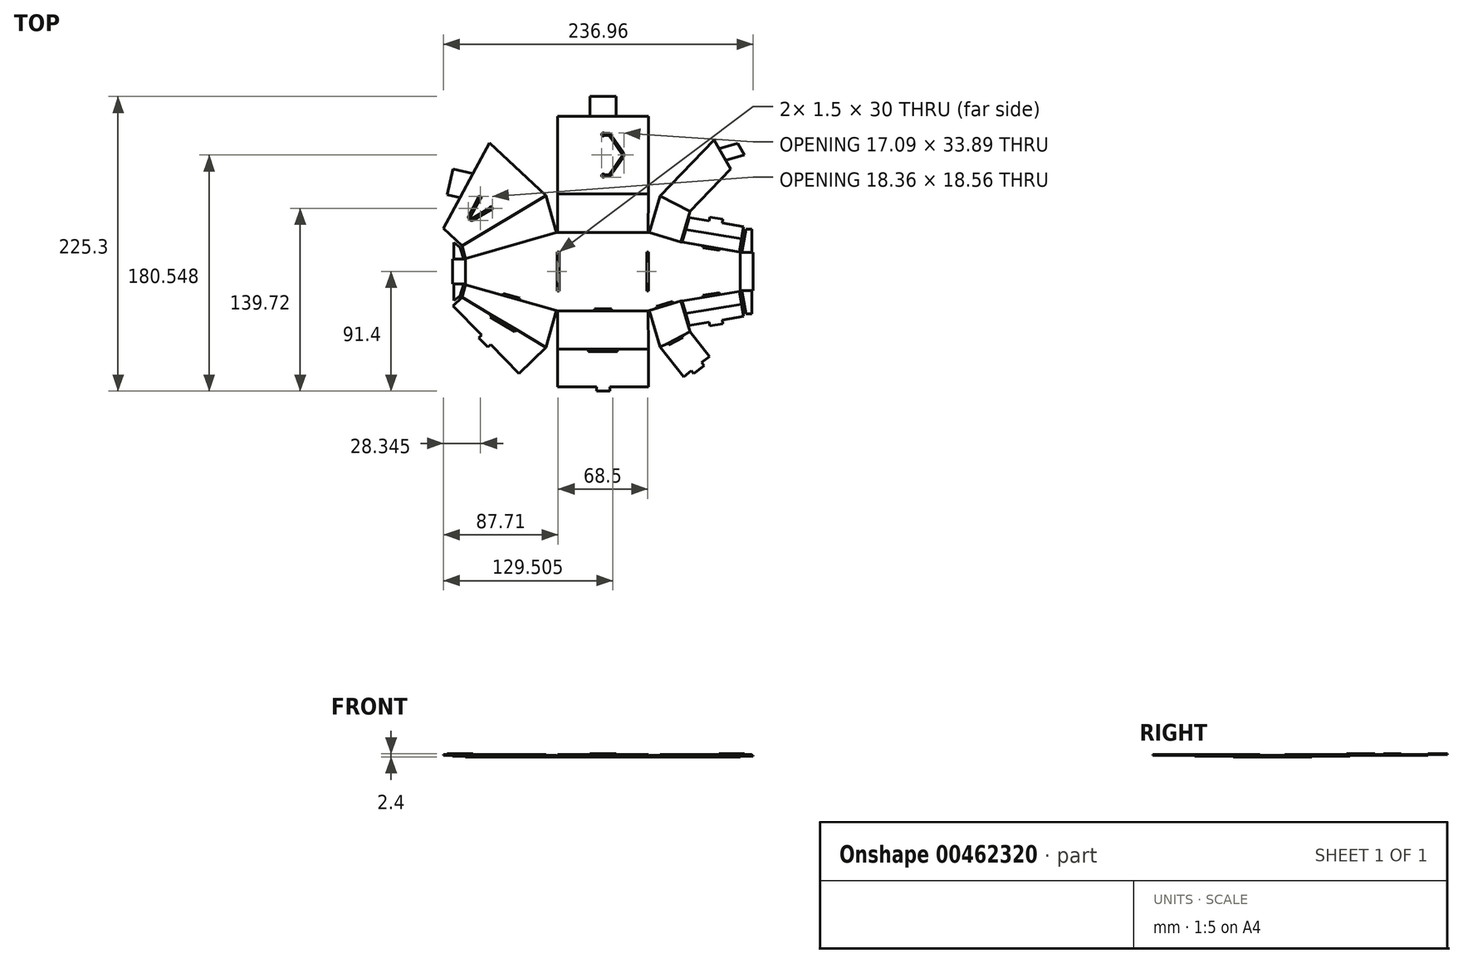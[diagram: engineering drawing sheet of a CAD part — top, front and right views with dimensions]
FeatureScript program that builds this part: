
annotation { "Feature Type Name" : "Feature", "Feature Type Description" : "" }
export const myFeature = defineFeature(function(context is Context, id is Id, definition is map)
    precondition{}
    {
        {
            var Q0;
            Q0=qCreatedBy(makeId("Top.planeOp"),FACE);
            var sketch = newSketch(context, id + "F0", { "sketchPlane" : qUnion([Q0])});
            skLineSegment(sketch, "E0.bottom", {"start": v(-35, 30) * mm, "end": v(35, 30) * mm});
            skLineSegment(sketch, "E0.top", {"start": v(-35, -30) * mm, "end": v(35, -30) * mm});
            skPoint(sketch, "E0.middle", {"position": v(0, 0) * mm});
            skLineSegment(sketch, "E1", {"start": v(-105, 0) * mm, "end": v(-105, 10) * mm});
            skLineSegment(sketch, "E2", {"start": v(-105, 10) * mm, "end": v(-35, 30) * mm});
            skLineSegment(sketch, "E3", {"start": v(-105, 0) * mm, "end": v(-105, -10) * mm});
            skLineSegment(sketch, "E4", {"start": v(-105, -10) * mm, "end": v(-35, -30) * mm});
            skLineSegment(sketch, "E5", {"start": v(60, -22.5) * mm, "end": v(35, -30) * mm});
            skLineSegment(sketch, "E6", {"start": v(60, 22.5) * mm, "end": v(35, 30) * mm});
            skLineSegment(sketch, "E7", {"start": v(105, 0) * mm, "end": v(105, 15) * mm});
            skLineSegment(sketch, "E8", {"start": v(105, 15) * mm, "end": v(60, 22.5) * mm});
            skLineSegment(sketch, "E9", {"start": v(105, 0) * mm, "end": v(105, -15) * mm});
            skLineSegment(sketch, "E10", {"start": v(105, -15) * mm, "end": v(60, -22.5) * mm});
            skSolve(sketch);
        }
        {
            var Q0;
            Q0 = qSketchRegion(id + "F0", true);
            extrude(context, id + "F1", {"entities" : qUnion([Q0]), "oppositeDirection" : true, "depth" : .6 * mm});
        }
        {
            var Q0;
            Q0=makeQuery(id+"F1.opExtrude","CAP_FACE",FACE,{"disambiguationData":[OSD([sQuery(id+"F0.wireOp",EDGE,"E0.bottom"),sQuery(id+"F0.wireOp",EDGE,"E0.top"),sQuery(id+"F0.wireOp",EDGE,"E1"),sQuery(id+"F0.wireOp",EDGE,"E2"),sQuery(id+"F0.wireOp",EDGE,"E3"),sQuery(id+"F0.wireOp",EDGE,"E4"),sQuery(id+"F0.wireOp",EDGE,"E5"),sQuery(id+"F0.wireOp",EDGE,"E6"),sQuery(id+"F0.wireOp",EDGE,"E7"),sQuery(id+"F0.wireOp",EDGE,"E8"),sQuery(id+"F0.wireOp",EDGE,"E9"),sQuery(id+"F0.wireOp",EDGE,"E10")])],"isStart":true});
            var sketch = newSketch(context, id + "F2", { "sketchPlane" : qUnion([Q0])});
            skLineSegment(sketch, "E11.0", {"start": v(-105, -10) * mm, "end": v(-35.48, -29.86) * mm});
            skPoint(sketch, "E12.orphan", {"position": v(-35, -30) * mm});
            skLineSegment(sketch, "E13", {"start": v(-35.48, -29.86) * mm, "end": v(-43.52, -58) * mm});
            skLineSegment(sketch, "E14", {"start": v(-105, -10) * mm, "end": v(-107.75, -19.62) * mm});
            skLineSegment(sketch, "E15", {"start": v(-107.75, -19.62) * mm, "end": v(-43.52, -58) * mm});
            skPoint(sketch, "E16.0", {"position": v(-105, 0) * mm});
            skLineSegment(sketch, "E17.MirrorCS", {"start": v(-105, 10) * mm, "end": v(-35.48, 29.86) * mm});
            skLineSegment(sketch, "E18.MirrorCS", {"start": v(-35.48, 29.86) * mm, "end": v(-43.52, 58) * mm});
            skLineSegment(sketch, "E19.MirrorCS", {"start": v(-107.75, 19.62) * mm, "end": v(-43.52, 58) * mm});
            skLineSegment(sketch, "E20.MirrorCS", {"start": v(-105, 10) * mm, "end": v(-107.75, 19.62) * mm});
            skSolve(sketch);
        }
        {
            var Q0;
            Q0 = qSketchRegion(id + "F2", true);
            extrude(context, id + "F3", {"entities" : qUnion([Q0]), "depth" : .6 * mm});
        }
        {
            var Q0;
            Q0=makeQuery(id+"F1.opExtrude","CAP_FACE",FACE,{"disambiguationData":[OSD([sQuery(id+"F0.wireOp",EDGE,"E0.bottom"),sQuery(id+"F0.wireOp",EDGE,"E0.top"),sQuery(id+"F0.wireOp",EDGE,"E1"),sQuery(id+"F0.wireOp",EDGE,"E2"),sQuery(id+"F0.wireOp",EDGE,"E3"),sQuery(id+"F0.wireOp",EDGE,"E4"),sQuery(id+"F0.wireOp",EDGE,"E5"),sQuery(id+"F0.wireOp",EDGE,"E6"),sQuery(id+"F0.wireOp",EDGE,"E7"),sQuery(id+"F0.wireOp",EDGE,"E8"),sQuery(id+"F0.wireOp",EDGE,"E9"),sQuery(id+"F0.wireOp",EDGE,"E10")])],"isStart":true});
            var sketch = newSketch(context, id + "F4", { "sketchPlane" : qUnion([Q0])});
            skLineSegment(sketch, "E21", {"start": v(34.5, 30) * mm, "end": v(35, 59.4) * mm});
            skLineSegment(sketch, "E22", {"start": v(-34.5, 30) * mm, "end": v(-34.5, 59.4) * mm});
            skLineSegment(sketch, "E23", {"start": v(-34.5, 59.4) * mm, "end": v(35, 59.4) * mm});
            skLineSegment(sketch, "E24", {"start": v(-34.5, 30) * mm, "end": v(34.5, 30) * mm});
            skLineSegment(sketch, "E25.MirrorCS", {"start": v(-34.5, -30) * mm, "end": v(34.5, -30) * mm});
            skLineSegment(sketch, "E26.MirrorCS", {"start": v(-34.5, -30) * mm, "end": v(-34.5, -59.4) * mm});
            skLineSegment(sketch, "E27.MirrorCS", {"start": v(-34.5, -59.4) * mm, "end": v(35, -59.4) * mm});
            skLineSegment(sketch, "E28.MirrorCS", {"start": v(34.5, -30) * mm, "end": v(35, -59.4) * mm});
            skSolve(sketch);
        }
        {
            var Q0;
            Q0 = qSketchRegion(id + "F4", true);
            extrude(context, id + "F5", {"entities" : qUnion([Q0]), "depth" : .6 * mm});
        }
        {
            var Q0;
            Q0=makeQuery(id+"F1.opExtrude","CAP_FACE",FACE,{"disambiguationData":[OSD([sQuery(id+"F0.wireOp",EDGE,"E0.bottom"),sQuery(id+"F0.wireOp",EDGE,"E0.top"),sQuery(id+"F0.wireOp",EDGE,"E1"),sQuery(id+"F0.wireOp",EDGE,"E2"),sQuery(id+"F0.wireOp",EDGE,"E3"),sQuery(id+"F0.wireOp",EDGE,"E4"),sQuery(id+"F0.wireOp",EDGE,"E5"),sQuery(id+"F0.wireOp",EDGE,"E6"),sQuery(id+"F0.wireOp",EDGE,"E7"),sQuery(id+"F0.wireOp",EDGE,"E8"),sQuery(id+"F0.wireOp",EDGE,"E9"),sQuery(id+"F0.wireOp",EDGE,"E10")])],"isStart":true});
            var sketch = newSketch(context, id + "F6", { "sketchPlane" : qUnion([Q0])});
            skLineSegment(sketch, "E29", {"start": v(59.52, -22.64) * mm, "end": v(66.56, -46.11) * mm});
            skLineSegment(sketch, "E30", {"start": v(35.48, -29.86) * mm, "end": v(43.9, -57.92) * mm});
            skPoint(sketch, "E31.orphan", {"position": v(60, -22.5) * mm});
            skLineSegment(sketch, "E32", {"start": v(35.48, -29.86) * mm, "end": v(59.52, -22.64) * mm});
            skLineSegment(sketch, "E33", {"start": v(66.56, -46.11) * mm, "end": v(43.9, -57.92) * mm});
            skPoint(sketch, "E34.endSnap0", {"position": v(105, 0) * mm});
            skLineSegment(sketch, "E35.MirrorCS", {"start": v(59.52, 22.64) * mm, "end": v(66.56, 46.11) * mm});
            skPoint(sketch, "E36.MirrorP", {"position": v(60, 22.5) * mm});
            skLineSegment(sketch, "E37.MirrorCS", {"start": v(35.48, 29.86) * mm, "end": v(59.52, 22.64) * mm});
            skLineSegment(sketch, "E38.MirrorCS", {"start": v(66.56, 46.11) * mm, "end": v(43.9, 57.92) * mm});
            skLineSegment(sketch, "E39.MirrorCS", {"start": v(35.48, 29.86) * mm, "end": v(43.9, 57.92) * mm});
            skSolve(sketch);
        }
        {
            var Q0;
            Q0 = qSketchRegion(id + "F6", true);
            extrude(context, id + "F7", {"entities" : qUnion([Q0]), "depth" : .6 * mm});
        }
        {
            var Q0;
            Q0=makeQuery(id+"F1.opExtrude","CAP_FACE",FACE,{"disambiguationData":[OSD([sQuery(id+"F0.wireOp",EDGE,"E0.bottom"),sQuery(id+"F0.wireOp",EDGE,"E0.top"),sQuery(id+"F0.wireOp",EDGE,"E1"),sQuery(id+"F0.wireOp",EDGE,"E2"),sQuery(id+"F0.wireOp",EDGE,"E3"),sQuery(id+"F0.wireOp",EDGE,"E4"),sQuery(id+"F0.wireOp",EDGE,"E5"),sQuery(id+"F0.wireOp",EDGE,"E6"),sQuery(id+"F0.wireOp",EDGE,"E7"),sQuery(id+"F0.wireOp",EDGE,"E8"),sQuery(id+"F0.wireOp",EDGE,"E9"),sQuery(id+"F0.wireOp",EDGE,"E10")])],"isStart":true});
            var sketch = newSketch(context, id + "F8", { "sketchPlane" : qUnion([Q0])});
            skLineSegment(sketch, "E40", {"start": v(104.5, -15.08) * mm, "end": v(106.15, -24.95) * mm});
            skLineSegment(sketch, "E41", {"start": v(106.15, -24.95) * mm, "end": v(63.39, -32.07) * mm});
            skLineSegment(sketch, "E42", {"start": v(60.5, -22.42) * mm, "end": v(63.39, -32.07) * mm});
            skLineSegment(sketch, "E43", {"start": v(60.5, -22.42) * mm, "end": v(104.5, -15.08) * mm});
            skLineSegment(sketch, "E44.MirrorCS", {"start": v(104.5, 15.08) * mm, "end": v(106.15, 24.95) * mm});
            skLineSegment(sketch, "E45.MirrorCS", {"start": v(106.15, 24.95) * mm, "end": v(63.39, 32.07) * mm});
            skLineSegment(sketch, "E46.MirrorCS", {"start": v(60.5, 22.42) * mm, "end": v(63.39, 32.07) * mm});
            skLineSegment(sketch, "E47.MirrorCS", {"start": v(60.5, 22.42) * mm, "end": v(104.5, 15.08) * mm});
            skSolve(sketch);
        }
        {
            var Q0;
            Q0 = qSketchRegion(id + "F8", true);
            extrude(context, id + "F9", {"entities" : qUnion([Q0]), "depth" : .6 * mm});
        }
        {
            var Q0;
            Q0=makeQuery(id+"F1.opExtrude","CAP_FACE",FACE,{"disambiguationData":[OSD([sQuery(id+"F0.wireOp",EDGE,"E0.bottom"),sQuery(id+"F0.wireOp",EDGE,"E0.top"),sQuery(id+"F0.wireOp",EDGE,"E1"),sQuery(id+"F0.wireOp",EDGE,"E2"),sQuery(id+"F0.wireOp",EDGE,"E3"),sQuery(id+"F0.wireOp",EDGE,"E4"),sQuery(id+"F0.wireOp",EDGE,"E5"),sQuery(id+"F0.wireOp",EDGE,"E6"),sQuery(id+"F0.wireOp",EDGE,"E7"),sQuery(id+"F0.wireOp",EDGE,"E8"),sQuery(id+"F0.wireOp",EDGE,"E9"),sQuery(id+"F0.wireOp",EDGE,"E10")])],"isStart":true});
            var sketch = newSketch(context, id + "F10", { "sketchPlane" : qUnion([Q0])});
            skLineSegment(sketch, "E48", {"start": v(-105, -9.5) * mm, "end": v(-115, -9.5) * mm});
            skLineSegment(sketch, "E49", {"start": v(-105, 9.5) * mm, "end": v(-115, 9.5) * mm});
            skLineSegment(sketch, "E50", {"start": v(-115, 9.5) * mm, "end": v(-115, -9.5) * mm});
            skLineSegment(sketch, "E51", {"start": v(-105, 9.5) * mm, "end": v(-105, -9.5) * mm});
            skSolve(sketch);
        }
        {
            var Q0;
            Q0 = qSketchRegion(id + "F10", true);
            extrude(context, id + "F11", {"entities" : qUnion([Q0]), "depth" : .6 * mm});
        }
        {
            var Q0;
            Q0=makeQuery(id+"F1.opExtrude","CAP_FACE",FACE,{"disambiguationData":[OSD([sQuery(id+"F0.wireOp",EDGE,"E0.bottom"),sQuery(id+"F0.wireOp",EDGE,"E0.top"),sQuery(id+"F0.wireOp",EDGE,"E1"),sQuery(id+"F0.wireOp",EDGE,"E2"),sQuery(id+"F0.wireOp",EDGE,"E3"),sQuery(id+"F0.wireOp",EDGE,"E4"),sQuery(id+"F0.wireOp",EDGE,"E5"),sQuery(id+"F0.wireOp",EDGE,"E6"),sQuery(id+"F0.wireOp",EDGE,"E7"),sQuery(id+"F0.wireOp",EDGE,"E8"),sQuery(id+"F0.wireOp",EDGE,"E9"),sQuery(id+"F0.wireOp",EDGE,"E10")])],"isStart":true});
            var sketch = newSketch(context, id + "F12", { "sketchPlane" : qUnion([Q0])});
            skLineSegment(sketch, "E52.0", {"start": v(105, 14.5) * mm, "end": v(105, -14.5) * mm});
            skLineSegment(sketch, "E53", {"start": v(105, 14.5) * mm, "end": v(115, 14.5) * mm});
            skLineSegment(sketch, "E54", {"start": v(115, 14.5) * mm, "end": v(115, -14.5) * mm});
            skLineSegment(sketch, "E55", {"start": v(115, -14.5) * mm, "end": v(105, -14.5) * mm});
            skPoint(sketch, "E56.orphan", {"position": v(105, -15) * mm});
            skPoint(sketch, "E57.orphan", {"position": v(105, 15) * mm});
            skSolve(sketch);
        }
        {
            var Q0;
            Q0 = qSketchRegion(id + "F12", true);
            extrude(context, id + "F13", {"entities" : qUnion([Q0]), "depth" : .6 * mm});
        }
        {
            var Q0;
            Q0=makeQuery(id+"F9.opExtrude","CAP_FACE",FACE,{"disambiguationData":[OSD([sQuery(id+"F8.wireOp",EDGE,"E44.MirrorCS"),sQuery(id+"F8.wireOp",EDGE,"E45.MirrorCS"),sQuery(id+"F8.wireOp",EDGE,"E46.MirrorCS"),sQuery(id+"F8.wireOp",EDGE,"E47.MirrorCS")])],"isStart":false});
            var sketch = newSketch(context, id + "F14", { "sketchPlane" : qUnion([Q0])});
            skLineSegment(sketch, "E58.0", {"start": v(106.15, 24.95) * mm, "end": v(63.39, 32.07) * mm});
            skLineSegment(sketch, "E59", {"start": v(91.26, 37.06) * mm, "end": v(107.71, 34.32) * mm});
            skLineSegment(sketch, "E60", {"start": v(63.39, 32.07) * mm, "end": v(66.14, 41.25) * mm});
            skLineSegment(sketch, "E61", {"start": v(81.4, 38.7) * mm, "end": v(66.14, 41.25) * mm});
            skLineSegment(sketch, "E62", {"start": v(106.15, 24.95) * mm, "end": v(107.71, 34.32) * mm});
            skPoint(sketch, "E63.orphan", {"position": v(121.18, 32.07) * mm});
            skLineSegment(sketch, "E64.0", {"start": v(86.83, 40.84) * mm, "end": v(91.76, 40.02) * mm});
            skLineSegment(sketch, "E65.0", {"start": v(86.83, 40.84) * mm, "end": v(81.9, 41.66) * mm});
            skLineSegment(sketch, "E66.0", {"start": v(91.26, 37.06) * mm, "end": v(91.76, 40.02) * mm});
            skLineSegment(sketch, "E67.0", {"start": v(81.4, 38.7) * mm, "end": v(81.9, 41.66) * mm});
            skPoint(sketch, "E68.start.orphan", {"position": v(84.77, 28.5) * mm});
            skLineSegment(sketch, "E69.MirrorCS", {"start": v(91.26, -37.06) * mm, "end": v(91.76, -40.02) * mm});
            skLineSegment(sketch, "E70.MirrorCS", {"start": v(81.4, -38.7) * mm, "end": v(81.9, -41.66) * mm});
            skLineSegment(sketch, "E71.MirrorCS", {"start": v(106.15, -24.95) * mm, "end": v(107.71, -34.32) * mm});
            skLineSegment(sketch, "E72.MirrorCS", {"start": v(63.39, -32.07) * mm, "end": v(66.14, -41.25) * mm});
            skLineSegment(sketch, "E73.MirrorCS", {"start": v(86.83, -40.84) * mm, "end": v(81.9, -41.66) * mm});
            skLineSegment(sketch, "E74.MirrorCS", {"start": v(106.15, -24.95) * mm, "end": v(63.39, -32.07) * mm});
            skPoint(sketch, "E75.MirrorP", {"position": v(84.77, -28.5) * mm});
            skLineSegment(sketch, "E76.MirrorCS", {"start": v(81.4, -38.7) * mm, "end": v(66.14, -41.25) * mm});
            skLineSegment(sketch, "E77.MirrorCS", {"start": v(91.26, -37.06) * mm, "end": v(107.71, -34.32) * mm});
            skLineSegment(sketch, "E78.MirrorCS", {"start": v(86.83, -40.84) * mm, "end": v(91.76, -40.02) * mm});
            skSolve(sketch);
        }
        {
            var Q0;
            Q0 = qSketchRegion(id + "F14", true);
            extrude(context, id + "F15", {"entities" : qUnion([Q0]), "depth" : .6 * mm});
        }
        {
            var Q0;
            Q0=makeQuery(id+"F13.opExtrude","CAP_FACE",FACE,{"disambiguationData":[OSD([sQuery(id+"F12.wireOp",EDGE,"E52.0"),sQuery(id+"F12.wireOp",EDGE,"E53"),sQuery(id+"F12.wireOp",EDGE,"E54"),sQuery(id+"F12.wireOp",EDGE,"E55")])],"isStart":false});
            var sketch = newSketch(context, id + "F16", { "sketchPlane" : qUnion([Q0])});
            skLineSegment(sketch, "E79", {"start": v(115, 14.5) * mm, "end": v(115, 32.5) * mm});
            skLineSegment(sketch, "E80", {"start": v(106.35, 14.5) * mm, "end": v(109.38, 32.5) * mm});
            skLineSegment(sketch, "E81", {"start": v(115, 32.5) * mm, "end": v(109.38, 32.5) * mm});
            skLineSegment(sketch, "E82", {"start": v(106.35, 14.5) * mm, "end": v(115, 14.5) * mm});
            skPoint(sketch, "E83.orphan", {"position": v(105, 32.5) * mm});
            skPoint(sketch, "E84.start.orphan", {"position": v(117.55, 14.5) * mm});
            skPoint(sketch, "E85.endSnap0", {"position": v(105, 0) * mm});
            skPoint(sketch, "E86.MirrorP", {"position": v(117.55, -14.5) * mm});
            skPoint(sketch, "E87.MirrorP", {"position": v(105, -32.5) * mm});
            skLineSegment(sketch, "E88.MirrorCS", {"start": v(115, -14.5) * mm, "end": v(115, -32.5) * mm});
            skLineSegment(sketch, "E89.MirrorCS", {"start": v(106.35, -14.5) * mm, "end": v(115, -14.5) * mm});
            skLineSegment(sketch, "E90.MirrorCS", {"start": v(115, -32.5) * mm, "end": v(109.38, -32.5) * mm});
            skLineSegment(sketch, "E91.MirrorCS", {"start": v(106.35, -14.5) * mm, "end": v(109.38, -32.5) * mm});
            skSolve(sketch);
        }
        {
            var Q0;
            Q0 = qSketchRegion(id + "F16", true);
            extrude(context, id + "F17", {"entities" : qUnion([Q0]), "depth" : .6 * mm});
        }
        {
            var Q0;
            Q0=makeQuery(id+"F1.opExtrude","CAP_FACE",FACE,{"disambiguationData":[OSD([sQuery(id+"F0.wireOp",EDGE,"E0.bottom"),sQuery(id+"F0.wireOp",EDGE,"E0.top"),sQuery(id+"F0.wireOp",EDGE,"E1"),sQuery(id+"F0.wireOp",EDGE,"E2"),sQuery(id+"F0.wireOp",EDGE,"E3"),sQuery(id+"F0.wireOp",EDGE,"E4"),sQuery(id+"F0.wireOp",EDGE,"E5"),sQuery(id+"F0.wireOp",EDGE,"E6"),sQuery(id+"F0.wireOp",EDGE,"E7"),sQuery(id+"F0.wireOp",EDGE,"E8"),sQuery(id+"F0.wireOp",EDGE,"E9"),sQuery(id+"F0.wireOp",EDGE,"E10")])],"isStart":true});
            var sketch = newSketch(context, id + "F18", { "sketchPlane" : qUnion([Q0])});
            skLineSegment(sketch, "E92.0", {"start": v(89.54, 17.58) * mm, "end": v(76.71, 19.71) * mm});
            skPoint(sketch, "E93.orphan", {"position": v(81.4, 38.7) * mm});
            skPoint(sketch, "E94.orphan", {"position": v(91.26, 37.06) * mm});
            skPoint(sketch, "E95.orphan", {"position": v(60.5, 22.42) * mm});
            skPoint(sketch, "E96.orphan", {"position": v(104.5, 15.08) * mm});
            skLineSegment(sketch, "E97.0", {"start": v(89.3, 16.1) * mm, "end": v(76.47, 18.23) * mm});
            skLineSegment(sketch, "E97.1", {"start": v(89.3, 16.1) * mm, "end": v(89.54, 17.58) * mm});
            skLineSegment(sketch, "E97.3", {"start": v(76.47, 18.23) * mm, "end": v(76.71, 19.71) * mm});
            skLineSegment(sketch, "E98.MirrorCS", {"start": v(89.3, -16.1) * mm, "end": v(89.54, -17.58) * mm});
            skLineSegment(sketch, "E99.MirrorCS", {"start": v(76.47, -18.23) * mm, "end": v(76.71, -19.71) * mm});
            skLineSegment(sketch, "E100.MirrorCS", {"start": v(89.54, -17.58) * mm, "end": v(76.71, -19.71) * mm});
            skLineSegment(sketch, "E101.MirrorCS", {"start": v(89.3, -16.1) * mm, "end": v(76.47, -18.23) * mm});
            skSolve(sketch);
        }
        {
            var Q0;
            Q0 = qSketchRegion(id + "F18", true);
            extrude(context, id + "F19", {"entities" : qUnion([Q0]), "operationType" : NewBodyOperationType.REMOVE, "oppositeDirection" : true, "depth" : 25 * mm});
        }
        {
            var Q0;
            Q0=makeQuery(id+"F5.opExtrude","CAP_FACE",FACE,{"disambiguationData":[OSD([sQuery(id+"F4.wireOp",EDGE,"E21"),sQuery(id+"F4.wireOp",EDGE,"E22"),sQuery(id+"F4.wireOp",EDGE,"E23"),sQuery(id+"F4.wireOp",EDGE,"E24")])],"isStart":false});
            var sketch = newSketch(context, id + "F20", { "sketchPlane" : qUnion([Q0])});
            skLineSegment(sketch, "E102.0", {"start": v(-34.5, 59.4) * mm, "end": v(35, 59.4) * mm});
            skLineSegment(sketch, "E103.0", {"start": v(-34.5, 118.9) * mm, "end": v(35, 118.9) * mm});
            skLineSegment(sketch, "E104", {"start": v(-34.5, 118.9) * mm, "end": v(-34.5, 59.4) * mm});
            skLineSegment(sketch, "E105", {"start": v(35, 118.9) * mm, "end": v(35, 59.4) * mm});
            skSolve(sketch);
        }
        {
            var Q0;
            Q0 = qSketchRegion(id + "F20", true);
            extrude(context, id + "F21", {"entities" : qUnion([Q0]), "depth" : .6 * mm});
        }
        {
            var Q0;
            Q0=makeQuery(id+"F21.opExtrude","CAP_FACE",FACE,{"disambiguationData":[OSD([sQuery(id+"F20.wireOp",EDGE,"E102.0"),sQuery(id+"F20.wireOp",EDGE,"E103.0"),sQuery(id+"F20.wireOp",EDGE,"E104"),sQuery(id+"F20.wireOp",EDGE,"E105")])],"isStart":false});
            var sketch = newSketch(context, id + "F22", { "sketchPlane" : qUnion([Q0])});
            skLineSegment(sketch, "E106.0", {"start": v(10.25, 118.9) * mm, "end": v(10.25, 133.9) * mm});
            skLineSegment(sketch, "E107.0", {"start": v(-9.75, 118.9) * mm, "end": v(-9.75, 133.9) * mm});
            skLineSegment(sketch, "E108", {"start": v(-9.75, 133.9) * mm, "end": v(10.25, 133.9) * mm});
            skLineSegment(sketch, "E109", {"start": v(-9.75, 118.9) * mm, "end": v(10.25, 118.9) * mm});
            skSolve(sketch);
        }
        {
            var Q0;
            Q0 = qSketchRegion(id + "F22", true);
            extrude(context, id + "F23", {"entities" : qUnion([Q0]), "operationType" : NewBodyOperationType.ADD, "depth" : .6 * mm});
        }
        {
            var Q0;
            Q0=makeQuery(id+"F5.opExtrude","CAP_FACE",FACE,{"disambiguationData":[OSD([sQuery(id+"F4.wireOp",EDGE,"E25.MirrorCS"),sQuery(id+"F4.wireOp",EDGE,"E26.MirrorCS"),sQuery(id+"F4.wireOp",EDGE,"E27.MirrorCS"),sQuery(id+"F4.wireOp",EDGE,"E28.MirrorCS")])],"isStart":false});
            var sketch = newSketch(context, id + "F24", { "sketchPlane" : qUnion([Q0])});
            skLineSegment(sketch, "E110.0", {"start": v(-34.5, -59.4) * mm, "end": v(-11, -59.4) * mm});
            skLineSegment(sketch, "E111.0", {"start": v(-34.5, -88.4) * mm, "end": v(-4.75, -88.4) * mm});
            skLineSegment(sketch, "E112", {"start": v(-34.5, -59.4) * mm, "end": v(-34.5, -88.4) * mm});
            skLineSegment(sketch, "E113", {"start": v(35, -59.4) * mm, "end": v(35, -88.4) * mm});
            skLineSegment(sketch, "E114.0", {"start": v(-4.75, -88.4) * mm, "end": v(-4.75, -91.4) * mm});
            skLineSegment(sketch, "E115.0", {"start": v(5.25, -88.4) * mm, "end": v(5.25, -91.4) * mm});
            skLineSegment(sketch, "E116", {"start": v(-4.75, -91.4) * mm, "end": v(5.25, -91.4) * mm});
            skLineSegment(sketch, "E117.trimOffspring", {"start": v(5.25, -88.4) * mm, "end": v(35, -88.4) * mm});
            skLineSegment(sketch, "E118", {"start": v(0, -61.4) * mm, "end": v(-11, -61.4) * mm});
            skLineSegment(sketch, "E119", {"start": v(0, -61.4) * mm, "end": v(11, -61.4) * mm});
            skLineSegment(sketch, "E120", {"start": v(-11, -61.4) * mm, "end": v(-11, -59.4) * mm});
            skLineSegment(sketch, "E121", {"start": v(11, -61.4) * mm, "end": v(11, -59.4) * mm});
            skLineSegment(sketch, "E122.trimOffspring", {"start": v(11, -59.4) * mm, "end": v(35, -59.4) * mm});
            skSolve(sketch);
        }
        {
            var Q0;
            Q0 = qSketchRegion(id + "F24", true);
            extrude(context, id + "F25", {"entities" : qUnion([Q0]), "depth" : .6 * mm});
        }
        {
            var Q0;
            Q0=makeQuery(id+"F3.opExtrude","CAP_FACE",FACE,{"disambiguationData":[OSD([sQuery(id+"F2.wireOp",EDGE,"E17.MirrorCS"),sQuery(id+"F2.wireOp",EDGE,"E18.MirrorCS"),sQuery(id+"F2.wireOp",EDGE,"E19.MirrorCS"),sQuery(id+"F2.wireOp",EDGE,"E20.MirrorCS")])],"isStart":false});
            var sketch = newSketch(context, id + "F26", { "sketchPlane" : qUnion([Q0])});
            skPoint(sketch, "E123.0", {"position": v(-35.48, 29.86) * mm});
            skPoint(sketch, "E124.0", {"position": v(-35.48, -29.86) * mm});
            skPoint(sketch, "E125.0", {"position": v(-105, 10) * mm});
            skPoint(sketch, "E126.0", {"position": v(-105, -10) * mm});
            skLineSegment(sketch, "E127.0", {"start": v(-107.75, 19.62) * mm, "end": v(-43.52, 58) * mm});
            skLineSegment(sketch, "E128", {"start": v(-43.52, 58) * mm, "end": v(-86.7, 98.53) * mm});
            skLineSegment(sketch, "E129", {"start": v(-107.75, 19.62) * mm, "end": v(-121.96, 32.96) * mm});
            skLineSegment(sketch, "E130", {"start": v(-86.7, 98.53) * mm, "end": v(-121.96, 32.96) * mm});
            skSolve(sketch);
        }
        {
            var Q0;
            Q0 = qSketchRegion(id + "F26", true);
            extrude(context, id + "F27", {"entities" : qUnion([Q0]), "depth" : .6 * mm});
        }
        {
            var Q0;
            Q0=makeQuery(id+"F1.opExtrude","CAP_FACE",FACE,{"disambiguationData":[OSD([sQuery(id+"F0.wireOp",EDGE,"E0.bottom"),sQuery(id+"F0.wireOp",EDGE,"E0.top"),sQuery(id+"F0.wireOp",EDGE,"E1"),sQuery(id+"F0.wireOp",EDGE,"E2"),sQuery(id+"F0.wireOp",EDGE,"E3"),sQuery(id+"F0.wireOp",EDGE,"E4"),sQuery(id+"F0.wireOp",EDGE,"E5"),sQuery(id+"F0.wireOp",EDGE,"E6"),sQuery(id+"F0.wireOp",EDGE,"E7"),sQuery(id+"F0.wireOp",EDGE,"E8"),sQuery(id+"F0.wireOp",EDGE,"E9"),sQuery(id+"F0.wireOp",EDGE,"E10")])],"isStart":true});
            var sketch = newSketch(context, id + "F28", { "sketchPlane" : qUnion([Q0])});
            skLineSegment(sketch, "E131.0", {"start": v(-6.25, -30) * mm, "end": v(6.75, -30) * mm});
            skPoint(sketch, "E132.orphan", {"position": v(-4.75, -91.4) * mm});
            skPoint(sketch, "E133.orphan", {"position": v(5.25, -91.4) * mm});
            skPoint(sketch, "E134.orphan", {"position": v(-34.5, -30) * mm});
            skPoint(sketch, "E135.orphan", {"position": v(34.5, -30) * mm});
            skLineSegment(sketch, "E136.0", {"start": v(6.75, -28.5) * mm, "end": v(6.75, -30) * mm});
            skLineSegment(sketch, "E136.1", {"start": v(-6.25, -28.5) * mm, "end": v(6.75, -28.5) * mm});
            skLineSegment(sketch, "E136.2", {"start": v(-6.25, -28.5) * mm, "end": v(-6.25, -30) * mm});
            skPoint(sketch, "E137.0.start.orphan", {"position": v(-4.75, -88.4) * mm});
            skPoint(sketch, "E138.0.start.orphan", {"position": v(5.25, -88.4) * mm});
            skSolve(sketch);
        }
        {
            var Q0;
            Q0 = qSketchRegion(id + "F28", true);
            extrude(context, id + "F29", {"entities" : qUnion([Q0]), "operationType" : NewBodyOperationType.REMOVE, "oppositeDirection" : true, "depth" : 25 * mm});
        }
        {
            var Q0;
            Q0=makeQuery(id+"F3.opExtrude","CAP_FACE",FACE,{"disambiguationData":[OSD([sQuery(id+"F2.wireOp",EDGE,"E11.0"),sQuery(id+"F2.wireOp",EDGE,"E13"),sQuery(id+"F2.wireOp",EDGE,"E14"),sQuery(id+"F2.wireOp",EDGE,"E15")])],"isStart":false});
            var sketch = newSketch(context, id + "F30", { "sketchPlane" : qUnion([Q0])});
            skLineSegment(sketch, "E139.0", {"start": v(-107.75, -19.62) * mm, "end": v(-85.08, -33.16) * mm});
            skLineSegment(sketch, "E140", {"start": v(-43.52, -58) * mm, "end": v(-64.13, -78.04) * mm});
            skLineSegment(sketch, "E141", {"start": v(-107.75, -19.62) * mm, "end": v(-114.55, -26.24) * mm});
            skLineSegment(sketch, "E142", {"start": v(-114.55, -26.24) * mm, "end": v(-92.83, -48.56) * mm});
            skLineSegment(sketch, "E143.0", {"start": v(-92.83, -48.56) * mm, "end": v(-94.98, -50.65) * mm});
            skLineSegment(sketch, "E144.0", {"start": v(-85.85, -55.72) * mm, "end": v(-88, -57.82) * mm});
            skLineSegment(sketch, "E145", {"start": v(-94.98, -50.65) * mm, "end": v(-88, -57.82) * mm});
            skLineSegment(sketch, "E146.trimOffspring", {"start": v(-85.85, -55.72) * mm, "end": v(-64.13, -78.04) * mm});
            skLineSegment(sketch, "E147.0", {"start": v(-85.08, -33.16) * mm, "end": v(-86.1, -34.88) * mm});
            skLineSegment(sketch, "E148.0", {"start": v(-66.2, -44.45) * mm, "end": v(-67.22, -46.16) * mm});
            skLineSegment(sketch, "E149", {"start": v(-86.1, -34.88) * mm, "end": v(-67.22, -46.16) * mm});
            skLineSegment(sketch, "E150.trimOffspring", {"start": v(-66.2, -44.45) * mm, "end": v(-43.52, -58) * mm});
            skSolve(sketch);
        }
        {
            var Q0;
            Q0 = qSketchRegion(id + "F30", true);
            extrude(context, id + "F31", {"entities" : qUnion([Q0]), "depth" : .6 * mm});
        }
        {
            var Q0;
            Q0=makeQuery(id+"F1.opExtrude","CAP_FACE",FACE,{"disambiguationData":[OSD([sQuery(id+"F0.wireOp",EDGE,"E0.bottom"),sQuery(id+"F0.wireOp",EDGE,"E0.top"),sQuery(id+"F0.wireOp",EDGE,"E1"),sQuery(id+"F0.wireOp",EDGE,"E2"),sQuery(id+"F0.wireOp",EDGE,"E3"),sQuery(id+"F0.wireOp",EDGE,"E4"),sQuery(id+"F0.wireOp",EDGE,"E5"),sQuery(id+"F0.wireOp",EDGE,"E6"),sQuery(id+"F0.wireOp",EDGE,"E7"),sQuery(id+"F0.wireOp",EDGE,"E8"),sQuery(id+"F0.wireOp",EDGE,"E9"),sQuery(id+"F0.wireOp",EDGE,"E10")])],"isStart":true});
            var sketch = newSketch(context, id + "F32", { "sketchPlane" : qUnion([Q0])});
            skLineSegment(sketch, "E151.0", {"start": v(-76.5, -18.15) * mm, "end": v(-64, -21.72) * mm});
            skLineSegment(sketch, "E152.0", {"start": v(-76.08, -16.7) * mm, "end": v(-63.58, -20.27) * mm});
            skLineSegment(sketch, "E153.0", {"start": v(-76.08, -16.7) * mm, "end": v(-76.5, -18.15) * mm});
            skLineSegment(sketch, "E154.0", {"start": v(-63.58, -20.27) * mm, "end": v(-64, -21.72) * mm});
            skPoint(sketch, "E155.end.orphan", {"position": v(-70.24, -19.93) * mm});
            skPoint(sketch, "E155.start.orphan", {"position": v(-69.83, -18.49) * mm});
            skSolve(sketch);
        }
        {
            var Q0;
            Q0 = qSketchRegion(id + "F32", true);
            extrude(context, id + "F33", {"entities" : qUnion([Q0]), "operationType" : NewBodyOperationType.REMOVE, "oppositeDirection" : true, "depth" : 25 * mm});
        }
        {
            var Q0;
            Q0=makeQuery(id+"F17.opExtrude","CAP_FACE",FACE,{"disambiguationData":[OSD([sQuery(id+"F16.wireOp",EDGE,"E79"),sQuery(id+"F16.wireOp",EDGE,"E80"),sQuery(id+"F16.wireOp",EDGE,"E81"),sQuery(id+"F16.wireOp",EDGE,"E82")])],"isStart":false});
            var sketch = newSketch(context, id + "F34", { "sketchPlane" : qUnion([Q0])});
            skPoint(sketch, "E156.0", {"position": v(115, 14.5) * mm});
            skLineSegment(sketch, "E157", {"start": v(115, 14.5) * mm, "end": v(114, 14.5) * mm});
            skLineSegment(sketch, "E158", {"start": v(114, 14.5) * mm, "end": v(114, 33.85) * mm});
            skLineSegment(sketch, "E159", {"start": v(114, 33.85) * mm, "end": v(116.35, 33.85) * mm});
            skLineSegment(sketch, "E160", {"start": v(116.35, 33.85) * mm, "end": v(116.35, -36.3) * mm});
            skPoint(sketch, "E161.0", {"position": v(115, -14.5) * mm});
            skLineSegment(sketch, "E162", {"start": v(115, -14.5) * mm, "end": v(114, -14.5) * mm});
            skLineSegment(sketch, "E163", {"start": v(114, -14.5) * mm, "end": v(114, -39.45) * mm});
            skLineSegment(sketch, "E164", {"start": v(115, 14.5) * mm, "end": v(115, -14.5) * mm});
            skLineSegment(sketch, "E165", {"start": v(114, -39.45) * mm, "end": v(116.35, -36.3) * mm});
            skSolve(sketch);
        }
        {
            var Q0;
            Q0 = qSketchRegion(id + "F34", true);
            extrude(context, id + "F35", {"entities" : qUnion([Q0]), "operationType" : NewBodyOperationType.REMOVE, "oppositeDirection" : true, "depth" : 25 * mm});
        }
        {
            var Q0;
            Q0=makeQuery(id+"F27.opExtrude","CAP_FACE",FACE,{"disambiguationData":[OSD([sQuery(id+"F26.wireOp",EDGE,"E127.0"),sQuery(id+"F26.wireOp",EDGE,"E128"),sQuery(id+"F26.wireOp",EDGE,"E129"),sQuery(id+"F26.wireOp",EDGE,"E130")])],"isStart":false});
            var sketch = newSketch(context, id + "F36", { "sketchPlane" : qUnion([Q0])});
            skLineSegment(sketch, "E166.0", {"start": v(-99.42, 74.88) * mm, "end": v(-114.52, 78.34) * mm});
            skLineSegment(sketch, "E167.0", {"start": v(-109.24, 56.61) * mm, "end": v(-118.99, 58.85) * mm});
            skLineSegment(sketch, "E168.0", {"start": v(-99.42, 74.88) * mm, "end": v(-109.24, 56.61) * mm});
            skLineSegment(sketch, "E169", {"start": v(-118.99, 58.85) * mm, "end": v(-114.52, 78.34) * mm});
            skSolve(sketch);
        }
        {
            var Q0;
            Q0 = qSketchRegion(id + "F36", true);
            extrude(context, id + "F37", {"entities" : qUnion([Q0]), "depth" : .6 * mm});
        }
        {
            var Q0;
            Q0=makeQuery(id+"F11.opExtrude","CAP_FACE",FACE,{"disambiguationData":[OSD([sQuery(id+"F10.wireOp",EDGE,"E48"),sQuery(id+"F10.wireOp",EDGE,"E49"),sQuery(id+"F10.wireOp",EDGE,"E50"),sQuery(id+"F10.wireOp",EDGE,"E51")])],"isStart":false});
            var sketch = newSketch(context, id + "F38", { "sketchPlane" : qUnion([Q0])});
            skLineSegment(sketch, "E170", {"start": v(-114, 9.5) * mm, "end": v(-114, 22.16) * mm});
            skLineSegment(sketch, "E171", {"start": v(-114, 22.16) * mm, "end": v(-109.13, 18.57) * mm});
            skLineSegment(sketch, "E172", {"start": v(-109.13, 18.57) * mm, "end": v(-106.39, 9.5) * mm});
            skLineSegment(sketch, "E173", {"start": v(-114, 9.5) * mm, "end": v(-106.39, 9.5) * mm});
            skLineSegment(sketch, "E174.MirrorCS", {"start": v(-114, -22.16) * mm, "end": v(-109.13, -18.57) * mm});
            skLineSegment(sketch, "E175.MirrorCS", {"start": v(-114, -9.5) * mm, "end": v(-114, -22.16) * mm});
            skLineSegment(sketch, "E176.MirrorCS", {"start": v(-114, -9.5) * mm, "end": v(-106.39, -9.5) * mm});
            skLineSegment(sketch, "E177.MirrorCS", {"start": v(-109.13, -18.57) * mm, "end": v(-106.39, -9.5) * mm});
            skSolve(sketch);
        }
        {
            var Q0;
            Q0 = qSketchRegion(id + "F38", true);
            extrude(context, id + "F39", {"entities" : qUnion([Q0]), "depth" : .6 * mm});
        }
        {
            var Q0;
            Q0=makeQuery(id+"F7.opExtrude","CAP_FACE",FACE,{"disambiguationData":[OSD([sQuery(id+"F6.wireOp",EDGE,"E29"),sQuery(id+"F6.wireOp",EDGE,"E30"),sQuery(id+"F6.wireOp",EDGE,"E32"),sQuery(id+"F6.wireOp",EDGE,"E33")])],"isStart":false});
            var sketch = newSketch(context, id + "F40", { "sketchPlane" : qUnion([Q0])});
            skLineSegment(sketch, "E178.0", {"start": v(66.56, -46.11) * mm, "end": v(43.9, -57.92) * mm});
            skLineSegment(sketch, "E179", {"start": v(66.56, -46.11) * mm, "end": v(81.45, -64.93) * mm});
            skLineSegment(sketch, "E180", {"start": v(43.9, -57.92) * mm, "end": v(61.77, -80.5) * mm});
            skLineSegment(sketch, "E181", {"start": v(81.45, -64.93) * mm, "end": v(75.53, -69.62) * mm});
            skLineSegment(sketch, "E182.0", {"start": v(67.69, -75.82) * mm, "end": v(69.55, -78.17) * mm});
            skLineSegment(sketch, "E183.0", {"start": v(75.53, -69.62) * mm, "end": v(77.4, -71.97) * mm});
            skLineSegment(sketch, "E184", {"start": v(77.4, -71.97) * mm, "end": v(69.55, -78.17) * mm});
            skLineSegment(sketch, "E185.trimOffspring", {"start": v(67.69, -75.82) * mm, "end": v(61.77, -80.5) * mm});
            skSolve(sketch);
        }
        {
            var Q0;
            Q0 = qSketchRegion(id + "F40", true);
            extrude(context, id + "F41", {"entities" : qUnion([Q0]), "depth" : .6 * mm});
        }
        {
            var Q0;
            Q0=makeQuery(id+"F7.opExtrude","CAP_FACE",FACE,{"disambiguationData":[OSD([sQuery(id+"F6.wireOp",EDGE,"E35.MirrorCS"),sQuery(id+"F6.wireOp",EDGE,"E37.MirrorCS"),sQuery(id+"F6.wireOp",EDGE,"E38.MirrorCS"),sQuery(id+"F6.wireOp",EDGE,"E39.MirrorCS")])],"isStart":false});
            var sketch = newSketch(context, id + "F42", { "sketchPlane" : qUnion([Q0])});
            skLineSegment(sketch, "E186", {"start": v(43.9, 57.92) * mm, "end": v(84.96, 100.56) * mm});
            skLineSegment(sketch, "E187", {"start": v(66.56, 46.11) * mm, "end": v(43.9, 57.92) * mm});
            skLineSegment(sketch, "E188", {"start": v(66.56, 46.11) * mm, "end": v(97.62, 78.37) * mm});
            skLineSegment(sketch, "E189", {"start": v(84.96, 100.56) * mm, "end": v(97.62, 78.37) * mm});
            skSolve(sketch);
        }
        {
            var Q0;
            Q0 = qSketchRegion(id + "F42", true);
            extrude(context, id + "F43", {"entities" : qUnion([Q0]), "depth" : .6 * mm});
        }
        {
            var Q0;
            Q0=makeQuery(id+"F43.opExtrude","CAP_FACE",FACE,{"disambiguationData":[OSD([sQuery(id+"F42.wireOp",EDGE,"E186"),sQuery(id+"F42.wireOp",EDGE,"E187"),sQuery(id+"F42.wireOp",EDGE,"E188"),sQuery(id+"F42.wireOp",EDGE,"E189")])],"isStart":false});
            var sketch = newSketch(context, id + "F44", { "sketchPlane" : qUnion([Q0])});
            skLineSegment(sketch, "E190.0", {"start": v(88.75, 93.92) * mm, "end": v(93.83, 85) * mm});
            skLineSegment(sketch, "E191.0", {"start": v(93.83, 85) * mm, "end": v(108.2, 89.32) * mm});
            skLineSegment(sketch, "E192.0", {"start": v(88.75, 93.92) * mm, "end": v(103.12, 98.23) * mm});
            skPoint(sketch, "E193.start.orphan", {"position": v(91.3, 89.47) * mm});
            skPoint(sketch, "E194.orphan", {"position": v(97.62, 78.37) * mm});
            skPoint(sketch, "E195.orphan", {"position": v(84.96, 100.56) * mm});
            skLineSegment(sketch, "E196", {"start": v(103.12, 98.23) * mm, "end": v(108.2, 89.32) * mm});
            skSolve(sketch);
        }
        {
            var Q0;
            Q0 = qSketchRegion(id + "F44", true);
            extrude(context, id + "F45", {"entities" : qUnion([Q0]), "depth" : .6 * mm});
        }
        {
            var Q0;
            Q0=makeQuery(id+"F41.opExtrude","CAP_FACE",FACE,{"disambiguationData":[OSD([sQuery(id+"F40.wireOp",EDGE,"E178.0"),sQuery(id+"F40.wireOp",EDGE,"E179"),sQuery(id+"F40.wireOp",EDGE,"E180"),sQuery(id+"F40.wireOp",EDGE,"E181"),sQuery(id+"F40.wireOp",EDGE,"E182.0"),sQuery(id+"F40.wireOp",EDGE,"E183.0"),sQuery(id+"F40.wireOp",EDGE,"E184"),sQuery(id+"F40.wireOp",EDGE,"E185.trimOffspring")])],"isStart":false});
            var sketch = newSketch(context, id + "F46", { "sketchPlane" : qUnion([Q0])});
            skLineSegment(sketch, "E197.0", {"start": v(60.55, -49.24) * mm, "end": v(49.9, -54.79) * mm});
            skLineSegment(sketch, "E198.0", {"start": v(60.55, -49.24) * mm, "end": v(61.24, -50.57) * mm});
            skLineSegment(sketch, "E199.0", {"start": v(49.9, -54.79) * mm, "end": v(50.6, -56.12) * mm});
            skPoint(sketch, "E200.orphan", {"position": v(43.9, -57.92) * mm});
            skPoint(sketch, "E201.orphan", {"position": v(66.56, -46.11) * mm});
            skLineSegment(sketch, "E202.0", {"start": v(61.24, -50.57) * mm, "end": v(50.6, -56.12) * mm});
            skSolve(sketch);
        }
        {
            var Q0;
            Q0 = qSketchRegion(id + "F46", true);
            extrude(context, id + "F47", {"entities" : qUnion([Q0]), "operationType" : NewBodyOperationType.REMOVE, "oppositeDirection" : true, "depth" : 25 * mm});
        }
        {
            var Q0;
            Q0=makeQuery(id+"F1.opExtrude","CAP_FACE",FACE,{"disambiguationData":[OSD([sQuery(id+"F0.wireOp",EDGE,"E0.bottom"),sQuery(id+"F0.wireOp",EDGE,"E0.top"),sQuery(id+"F0.wireOp",EDGE,"E1"),sQuery(id+"F0.wireOp",EDGE,"E2"),sQuery(id+"F0.wireOp",EDGE,"E3"),sQuery(id+"F0.wireOp",EDGE,"E4"),sQuery(id+"F0.wireOp",EDGE,"E5"),sQuery(id+"F0.wireOp",EDGE,"E6"),sQuery(id+"F0.wireOp",EDGE,"E7"),sQuery(id+"F0.wireOp",EDGE,"E8"),sQuery(id+"F0.wireOp",EDGE,"E9"),sQuery(id+"F0.wireOp",EDGE,"E10")])],"isStart":true});
            var sketch = newSketch(context, id + "F48", { "sketchPlane" : qUnion([Q0])});
            skLineSegment(sketch, "E203.0", {"start": v(53.73, -24.38) * mm, "end": v(41.27, -28.12) * mm});
            skLineSegment(sketch, "E204.0", {"start": v(53.3, -22.95) * mm, "end": v(40.84, -26.68) * mm});
            skPoint(sketch, "E205.end.orphan", {"position": v(47.07, -24.81) * mm});
            skPoint(sketch, "E205.start.orphan", {"position": v(47.5, -26.25) * mm});
            skLineSegment(sketch, "E206.0", {"start": v(40.84, -26.68) * mm, "end": v(41.27, -28.12) * mm});
            skLineSegment(sketch, "E207.0", {"start": v(53.3, -22.95) * mm, "end": v(53.73, -24.38) * mm});
            skPoint(sketch, "E208.orphan", {"position": v(35.05, -28.42) * mm});
            skPoint(sketch, "E209.orphan", {"position": v(35.48, -29.86) * mm});
            skPoint(sketch, "E210.orphan", {"position": v(59.52, -22.64) * mm});
            skPoint(sketch, "E211.orphan", {"position": v(59.1, -21.2) * mm});
            skSolve(sketch);
        }
        {
            var Q0;
            Q0 = qSketchRegion(id + "F48", true);
            extrude(context, id + "F49", {"entities" : qUnion([Q0]), "operationType" : NewBodyOperationType.REMOVE, "oppositeDirection" : true, "depth" : 25 * mm});
        }
        {
            var Q0;
            Q0=makeQuery(id+"F21.opExtrude","CAP_FACE",FACE,{"disambiguationData":[OSD([sQuery(id+"F20.wireOp",EDGE,"E102.0"),sQuery(id+"F20.wireOp",EDGE,"E103.0"),sQuery(id+"F20.wireOp",EDGE,"E104"),sQuery(id+"F20.wireOp",EDGE,"E105")])],"isStart":false});
            var sketch = newSketch(context, id + "F50", { "sketchPlane" : qUnion([Q0])});
            skPoint(sketch, "E212.0", {"position": v(0.25, 118.9) * mm});
            skPoint(sketch, "E212.1", {"position": v(-34.5, 89.15) * mm});
            skPoint(sketch, "E212.2", {"position": v(0.25, 59.4) * mm});
            skPoint(sketch, "E212.3", {"position": v(35, 89.15) * mm});
            skLineSegment(sketch, "E213.0", {"start": v(4.75, 104.15) * mm, "end": v(1.25, 104.15) * mm});
            skLineSegment(sketch, "E214.0", {"start": v(4.74, 74.15) * mm, "end": v(1.25, 74.15) * mm});
            skLineSegment(sketch, "E215", {"start": v(14.05, 90.87) * mm, "end": v(4.75, 104.15) * mm});
            skLineSegment(sketch, "E216", {"start": v(14.05, 87.43) * mm, "end": v(4.74, 74.15) * mm});
            skPoint(sketch, "E217.visualSharp", {"position": v(15.25, 89.15) * mm});
            skArc(sketch, "E217.filletArc", {"start": v(14.05, 87.43) * mm, "mid": v(14.59, 89.15) * mm, "end": v(14.05, 90.87) * mm});
            skLineSegment(sketch, "E218.0", {"start": v(5.53, 105.65) * mm, "end": v(1.25, 105.65) * mm});
            skLineSegment(sketch, "E218.1", {"start": v(5.53, 72.65) * mm, "end": v(1.25, 72.65) * mm});
            skLineSegment(sketch, "E218.2", {"start": v(15.28, 86.57) * mm, "end": v(5.53, 72.65) * mm});
            skArc(sketch, "E218.3", {"start": v(15.28, 86.57) * mm, "mid": v(16.09, 89.15) * mm, "end": v(15.28, 91.73) * mm});
            skLineSegment(sketch, "E218.4", {"start": v(15.28, 91.73) * mm, "end": v(5.53, 105.65) * mm});
            skArc(sketch, "E219", {"start": v(1.25, 105.65) * mm, "mid": v(-1, 104.9) * mm, "end": v(1.25, 104.15) * mm});
            skArc(sketch, "E220", {"start": v(1.25, 74.15) * mm, "mid": v(-1, 73.4) * mm, "end": v(1.25, 72.65) * mm});
            skPoint(sketch, "E221.orphan", {"position": v(0.25, 105.65) * mm});
            skPoint(sketch, "E222.orphan", {"position": v(0.25, 104.15) * mm});
            skPoint(sketch, "E223.orphan", {"position": v(0.25, 74.15) * mm});
            skPoint(sketch, "E224.orphan", {"position": v(0.25, 72.65) * mm});
            skSolve(sketch);
        }
        {
            var Q0;
            Q0 = qSketchRegion(id + "F50", true);
            extrude(context, id + "F51", {"entities" : qUnion([Q0]), "operationType" : NewBodyOperationType.REMOVE, "oppositeDirection" : true, "depth" : 25 * mm});
        }
        {
            var Q0;
            Q0=makeQuery(id+"F27.opExtrude","CAP_FACE",FACE,{"disambiguationData":[OSD([sQuery(id+"F26.wireOp",EDGE,"E127.0"),sQuery(id+"F26.wireOp",EDGE,"E128"),sQuery(id+"F26.wireOp",EDGE,"E129"),sQuery(id+"F26.wireOp",EDGE,"E130")])],"isStart":false});
            var sketch = newSketch(context, id + "F52", { "sketchPlane" : qUnion([Q0])});
            skLineSegment(sketch, "E225.0", {"start": v(-94.15, 55.13) * mm, "end": v(-101.2, 42) * mm});
            skLineSegment(sketch, "E226.0", {"start": v(-99.81, 40.66) * mm, "end": v(-86.92, 48.37) * mm});
            skPoint(sketch, "E227.visualSharp", {"position": v(-102.92, 38.8) * mm});
            skArc(sketch, "E227.filletArc", {"start": v(-101.2, 42) * mm, "mid": v(-101.02, 40.8) * mm, "end": v(-99.81, 40.66) * mm});
            skLineSegment(sketch, "E228.0", {"start": v(-99.04, 39.38) * mm, "end": v(-86.15, 47.08) * mm});
            skArc(sketch, "E228.1", {"start": v(-102.53, 42.7) * mm, "mid": v(-102.05, 39.72) * mm, "end": v(-99.04, 39.38) * mm});
            skLineSegment(sketch, "E228.2", {"start": v(-95.47, 55.84) * mm, "end": v(-102.53, 42.7) * mm});
            skPoint(sketch, "E229.orphan", {"position": v(-104.33, 65.75) * mm});
            skPoint(sketch, "E230.orphan", {"position": v(-75.63, 38.8) * mm});
            skArc(sketch, "E231", {"start": v(-94.15, 55.13) * mm, "mid": v(-93.74, 57.46) * mm, "end": v(-95.47, 55.84) * mm});
            skArc(sketch, "E232", {"start": v(-86.15, 47.08) * mm, "mid": v(-84.6, 48.88) * mm, "end": v(-86.92, 48.37) * mm});
            skPoint(sketch, "E233.orphan", {"position": v(-94.9, 56.9) * mm});
            skPoint(sketch, "E234.orphan", {"position": v(-93.77, 55.83) * mm});
            skPoint(sketch, "E235.orphan", {"position": v(-85.11, 47.7) * mm});
            skPoint(sketch, "E236.orphan", {"position": v(-86.25, 48.77) * mm});
            skSolve(sketch);
        }
        {
            var Q0;
            Q0 = qSketchRegion(id + "F52", true);
            extrude(context, id + "F53", {"entities" : qUnion([Q0]), "operationType" : NewBodyOperationType.REMOVE, "oppositeDirection" : true, "depth" : 25 * mm});
        }
        {
            var Q0;
            Q0=makeQuery(id+"F1.opExtrude","CAP_FACE",FACE,{"disambiguationData":[OSD([sQuery(id+"F0.wireOp",EDGE,"E0.bottom"),sQuery(id+"F0.wireOp",EDGE,"E0.top"),sQuery(id+"F0.wireOp",EDGE,"E1"),sQuery(id+"F0.wireOp",EDGE,"E2"),sQuery(id+"F0.wireOp",EDGE,"E3"),sQuery(id+"F0.wireOp",EDGE,"E4"),sQuery(id+"F0.wireOp",EDGE,"E5"),sQuery(id+"F0.wireOp",EDGE,"E6"),sQuery(id+"F0.wireOp",EDGE,"E7"),sQuery(id+"F0.wireOp",EDGE,"E8"),sQuery(id+"F0.wireOp",EDGE,"E9"),sQuery(id+"F0.wireOp",EDGE,"E10")])],"isStart":true});
            var sketch = newSketch(context, id + "F54", { "sketchPlane" : qUnion([Q0])});
            skLineSegment(sketch, "E237", {"start": v(-35, 15) * mm, "end": v(-35, -15) * mm});
            skLineSegment(sketch, "E238", {"start": v(35, 15) * mm, "end": v(35, -15) * mm});
            skLineSegment(sketch, "E239.0", {"start": v(-33.5, 15) * mm, "end": v(-33.5, -15) * mm});
            skLineSegment(sketch, "E240.0", {"start": v(33.5, 15) * mm, "end": v(33.5, -15) * mm});
            skLineSegment(sketch, "E241.0", {"start": v(-35, -15) * mm, "end": v(-33.5, -15) * mm});
            skLineSegment(sketch, "E242.0", {"start": v(-35, 15) * mm, "end": v(-33.5, 15) * mm});
            skLineSegment(sketch, "E243.trimOffspring", {"start": v(33.5, 15) * mm, "end": v(35, 15) * mm});
            skPoint(sketch, "E244.orphan", {"position": v(-35, 30) * mm});
            skPoint(sketch, "E245.orphan", {"position": v(-35, -30) * mm});
            skPoint(sketch, "E246.orphan", {"position": v(35, -30) * mm});
            skPoint(sketch, "E247.orphan", {"position": v(35, 30) * mm});
            skLineSegment(sketch, "E248.trimOffspring", {"start": v(33.5, -15) * mm, "end": v(35, -15) * mm});
            skSolve(sketch);
        }
        {
            var Q0;
            Q0 = qSketchRegion(id + "F54", true);
            extrude(context, id + "F55", {"entities" : qUnion([Q0]), "operationType" : NewBodyOperationType.REMOVE, "oppositeDirection" : true, "depth" : 25 * mm});
        }
    });
